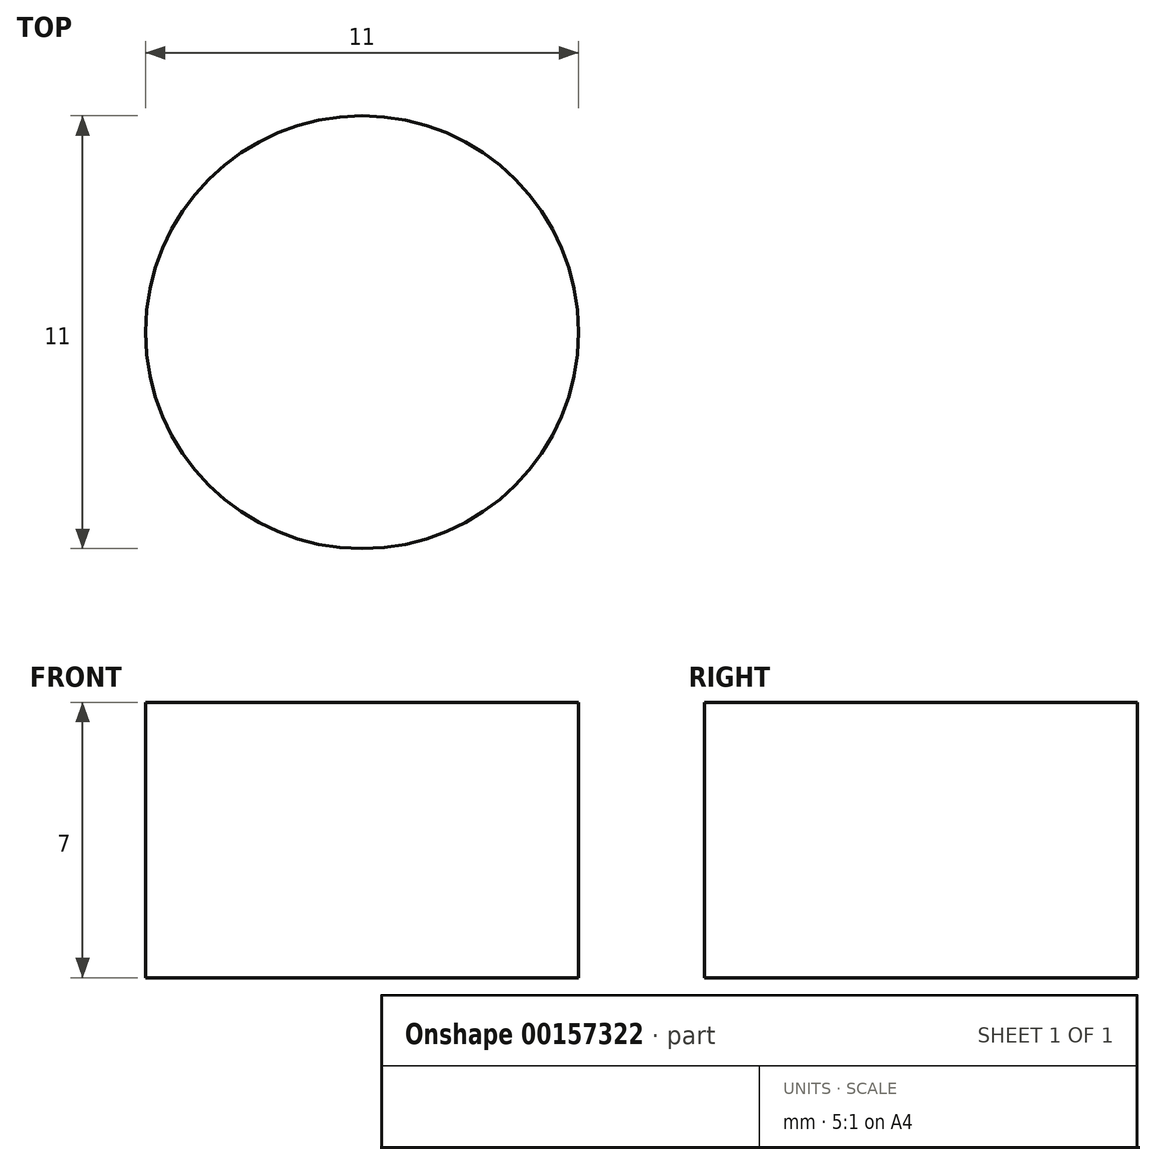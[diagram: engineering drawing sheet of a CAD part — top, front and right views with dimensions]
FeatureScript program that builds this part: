
annotation { "Feature Type Name" : "Feature", "Feature Type Description" : "" }
export const myFeature = defineFeature(function(context is Context, id is Id, definition is map)
    precondition{}
    {
        {
            var Q0;
            Q0=qCreatedBy(makeId("Front.planeOp"),FACE);
            var sketch = newSketch(context, id + "F0", { "sketchPlane" : qUnion([Q0])});
            skLineSegment(sketch, "E0", {"start": v(0, 0) * mm, "end": v(19, 0) * mm});
            skLineSegment(sketch, "E1", {"start": v(19, 0) * mm, "end": v(19, 4.9) * mm});
            skLineSegment(sketch, "E2", {"start": v(19, 4.9) * mm, "end": v(14.5, 4.9) * mm});
            skLineSegment(sketch, "E3", {"start": v(14.5, 4.9) * mm, "end": v(14.5, 7) * mm});
            skLineSegment(sketch, "E4", {"start": v(14.5, 7) * mm, "end": v(0, 7) * mm});
            skLineSegment(sketch, "E5", {"start": v(0, 7) * mm, "end": v(0, 0) * mm});
            skLineSegment(sketch, "E6.bottom", {"start": v(0, 7) * mm, "end": v(5.5, 7) * mm});
            skLineSegment(sketch, "E6.top", {"start": v(0, 0) * mm, "end": v(5.5, 0) * mm});
            skLineSegment(sketch, "E6.right", {"start": v(5.5, 7) * mm, "end": v(5.5, 0) * mm});
            skSolve(sketch);
        }
        {
            var Q0;
            Q0=makeQuery(id+"F0.imprint","IMPRINT",FACE,{"disambiguationData":[TD([[makeQuery(id+"F0.imprint","IMPRINT",EDGE,{"derivedFrom":sQuery(id+"F0.wireOp",EDGE,"E0")}),1.0]])]});
            var Q1;
            Q1=sQuery(id+"F0.wireOp",EDGE,"E5");
            revolve(context, id + "F1", {"entities" : qUnion([Q0]), "axis" : qUnion([Q1]), "revolveType" : RevolveType.FULL});
        }
    });
